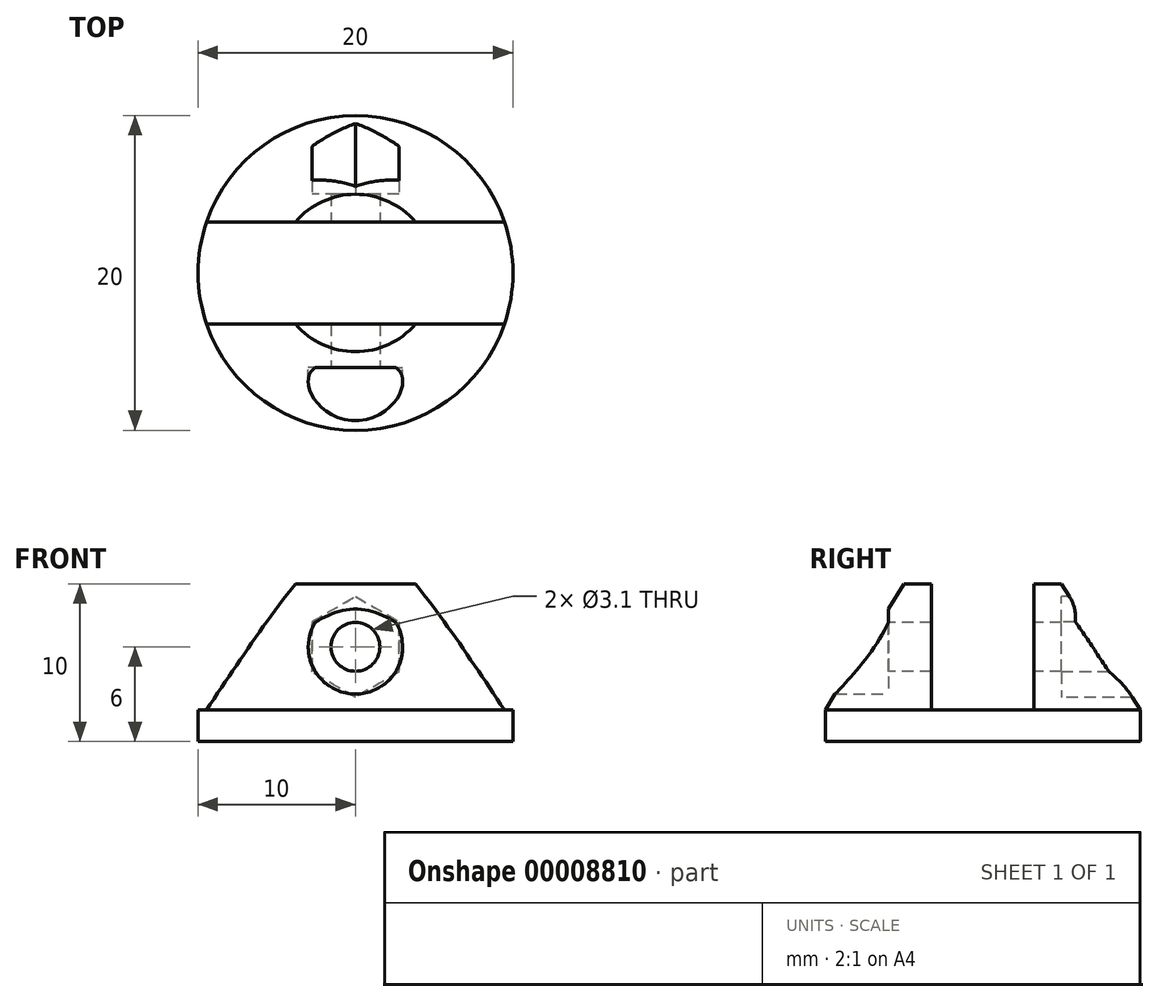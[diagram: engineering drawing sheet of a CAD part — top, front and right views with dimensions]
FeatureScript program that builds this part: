
annotation { "Feature Type Name" : "Feature", "Feature Type Description" : "" }
export const myFeature = defineFeature(function(context is Context, id is Id, definition is map)
    precondition{}
    {
        {
            var Q0;
            Q0=qCreatedBy(makeId("Top.planeOp"),FACE);
            var sketch = newSketch(context, id + "F0", { "sketchPlane" : qUnion([Q0])});
            skCircle(sketch, "E0", {"center": v(0, 0) * mm, "radius": 10 * mm});
            skSolve(sketch);
        }
        {
            var Q0;
            Q0=makeQuery(id+"F0.imprint","IMPRINT",FACE,{"disambiguationData":[TD([[makeQuery(id+"F0.imprint","IMPRINT",EDGE,{"derivedFrom":sQuery(id+"F0.wireOp",EDGE,"E0")}),1.0]])]});
            extrude(context, id + "F1", {"entities" : qUnion([Q0]), "depth" : 10 * mm});
        }
        {
            var Q0;
            Q0=makeQuery(id+"F1.opExtrude","CAP_FACE",FACE,{"disambiguationData":[OSD([sQuery(id+"F0.wireOp",EDGE,"E0")])],"isStart":false});
            var sketch = newSketch(context, id + "F2", { "sketchPlane" : qUnion([Q0])});
            skLineSegment(sketch, "E1.bottom", {"start": v(-11.7, 3.25) * mm, "end": v(11.7, 3.25) * mm});
            skLineSegment(sketch, "E1.top", {"start": v(-11.7, -3.25) * mm, "end": v(11.7, -3.25) * mm});
            skLineSegment(sketch, "E1.left", {"start": v(-11.7, 3.25) * mm, "end": v(-11.7, -3.25) * mm});
            skLineSegment(sketch, "E1.right", {"start": v(11.7, 3.25) * mm, "end": v(11.7, -3.25) * mm});
            skSolve(sketch);
        }
        {
            var Q0;
            {var subQ0=makeQuery(id+"F1.opExtrude","CAP_EDGE",EDGE,{"disambiguationData":[OSD([sQuery(id+"F0.wireOp",EDGE,"E0")])],"isStart":false});var subQ3=sQuery(id+"F2.wireOp",EDGE,"E1.bottom");var subQ6=makeQuery(id+"F2.imprint","INTERSECT",VERTEX,{"disambiguationData":[OD(0.0)],"derivedFrom":[subQ0,subQ3]});Q0=makeQuery(id+"F2.imprint","IMPRINT",FACE,{"disambiguationData":[TD([[makeQuery(id+"F2.imprint","IMPRINT",EDGE,{"disambiguationData":[TD([[subQ6,-1.0]])],"derivedFrom":subQ3}),-1.0]])]});}
            extrude(context, id + "F3", {"entities" : qUnion([Q0]), "operationType" : NewBodyOperationType.REMOVE, "oppositeDirection" : true, "depth" : 8 * mm});
        }
        {
            var Q0;
            {var subQ0=sQuery(id+"F0.wireOp",EDGE,"E0");Q0=makeQuery(id+"F3.boolean.opBoolean","SPLIT",EDGE,{"disambiguationData":[TD([makeQuery(id+"F3.opExtrude","SWEPT_FACE",FACE,{"disambiguationData":[OSD([sQuery(id+"F2.wireOp",EDGE,"E1.top")])]})])],"derivedFrom":makeQuery(id+"F1.opExtrude","CAP_EDGE",EDGE,{"disambiguationData":[OSD([subQ0])],"isStart":false})});}
            var Q1;
            {var subQ0=sQuery(id+"F0.wireOp",EDGE,"E0");Q1=makeQuery(id+"F3.boolean.opBoolean","SPLIT",EDGE,{"disambiguationData":[TD([makeQuery(id+"F3.opExtrude","SWEPT_FACE",FACE,{"disambiguationData":[OSD([sQuery(id+"F2.wireOp",EDGE,"E1.bottom")])]})])],"derivedFrom":makeQuery(id+"F1.opExtrude","CAP_EDGE",EDGE,{"disambiguationData":[OSD([subQ0])],"isStart":false})});}
            chamfer(context, id + "F4", {"entities" : qUnion([Q0, Q1]), "chamferType" : ChamferType.TWO_OFFSETS, "width1" : 5 * mm, "oppositeDirection" : false, "width2" : 8 * mm, "tangentPropagation" : true});
        }
        {
            var Q0;
            Q0=qCreatedBy(makeId("Front.planeOp"),FACE);
            var sketch = newSketch(context, id + "F5", { "sketchPlane" : qUnion([Q0])});
            skCircle(sketch, "E2", {"center": v(0, 6) * mm, "radius": 1.55 * mm});
            skSolve(sketch);
        }
        {
            var Q0;
            Q0=makeQuery(id+"F5.imprint","IMPRINT",FACE,{"disambiguationData":[TD([[makeQuery(id+"F5.imprint","IMPRINT",EDGE,{"derivedFrom":sQuery(id+"F5.wireOp",EDGE,"E2")}),1.0]])]});
            var Q1;
            Q1=sQuery(id+"F5.wireOp",EDGE,"E2");
            extrude(context, id + "F6", {"entities" : qUnion([Q0]), "operationType" : NewBodyOperationType.REMOVE, "surfaceEntities" : qUnion([Q1]), "endBound" : BoundingType.SYMMETRIC, "oppositeDirection" : true, "depth" : 25 * mm});
        }
        {
            var Q0;
            Q0=qCreatedBy(makeId("Front.planeOp"),FACE);
            var sketch = newSketch(context, id + "F7", { "sketchPlane" : qUnion([Q0])});
            skCircle(sketch, "E3", {"center": v(0, 6) * mm, "radius": 3 * mm});
            skSolve(sketch);
        }
        {
            var Q0;
            Q0=makeQuery(id+"F7.imprint","IMPRINT",FACE,{"disambiguationData":[TD([[makeQuery(id+"F7.imprint","IMPRINT",EDGE,{"derivedFrom":sQuery(id+"F7.wireOp",EDGE,"E3")}),1.0]])]});
            extrude(context, id + "F8", {"entities" : qUnion([Q0]), "operationType" : NewBodyOperationType.REMOVE, "depth" : 25 * mm, "hasSecondDirection" : true, "secondDirectionOppositeDirection" : false, "secondDirectionDepth" : 6 * mm});
        }
        {
            var Q0;
            Q0=qCreatedBy(makeId("Front.planeOp"),FACE);
            var sketch = newSketch(context, id + "F9", { "sketchPlane" : qUnion([Q0])});
            skCircle(sketch, "E4.cCircle", {"center": v(0, 6) * mm, "radius": 3.2 * mm, "construction": true});
            skLineSegment(sketch, "E4.0", {"start": v(2.77, 4.4) * mm, "end": v(0, 2.8) * mm});
            skLineSegment(sketch, "E4.1", {"start": v(0, 2.8) * mm, "end": v(-2.77, 4.4) * mm});
            skLineSegment(sketch, "E4.2", {"start": v(-2.77, 4.4) * mm, "end": v(-2.77, 7.6) * mm});
            skLineSegment(sketch, "E4.3", {"start": v(-2.77, 7.6) * mm, "end": v(0, 9.2) * mm});
            skLineSegment(sketch, "E4.4", {"start": v(0, 9.2) * mm, "end": v(2.77, 7.6) * mm});
            skLineSegment(sketch, "E4.5", {"start": v(2.77, 7.6) * mm, "end": v(2.77, 4.4) * mm});
            skSolve(sketch);
        }
        {
            var Q0;
            Q0=makeQuery(id+"F9.imprint","IMPRINT",FACE,{"disambiguationData":[TD([[makeQuery(id+"F9.imprint","IMPRINT",EDGE,{"derivedFrom":sQuery(id+"F9.wireOp",EDGE,"E4.0")}),-1.0]])]});
            extrude(context, id + "F10", {"entities" : qUnion([Q0]), "operationType" : NewBodyOperationType.REMOVE, "oppositeDirection" : true, "depth" : 25 * mm, "hasSecondDirection" : true, "secondDirectionOppositeDirection" : true, "secondDirectionDepth" : 5 * mm});
        }
    });
